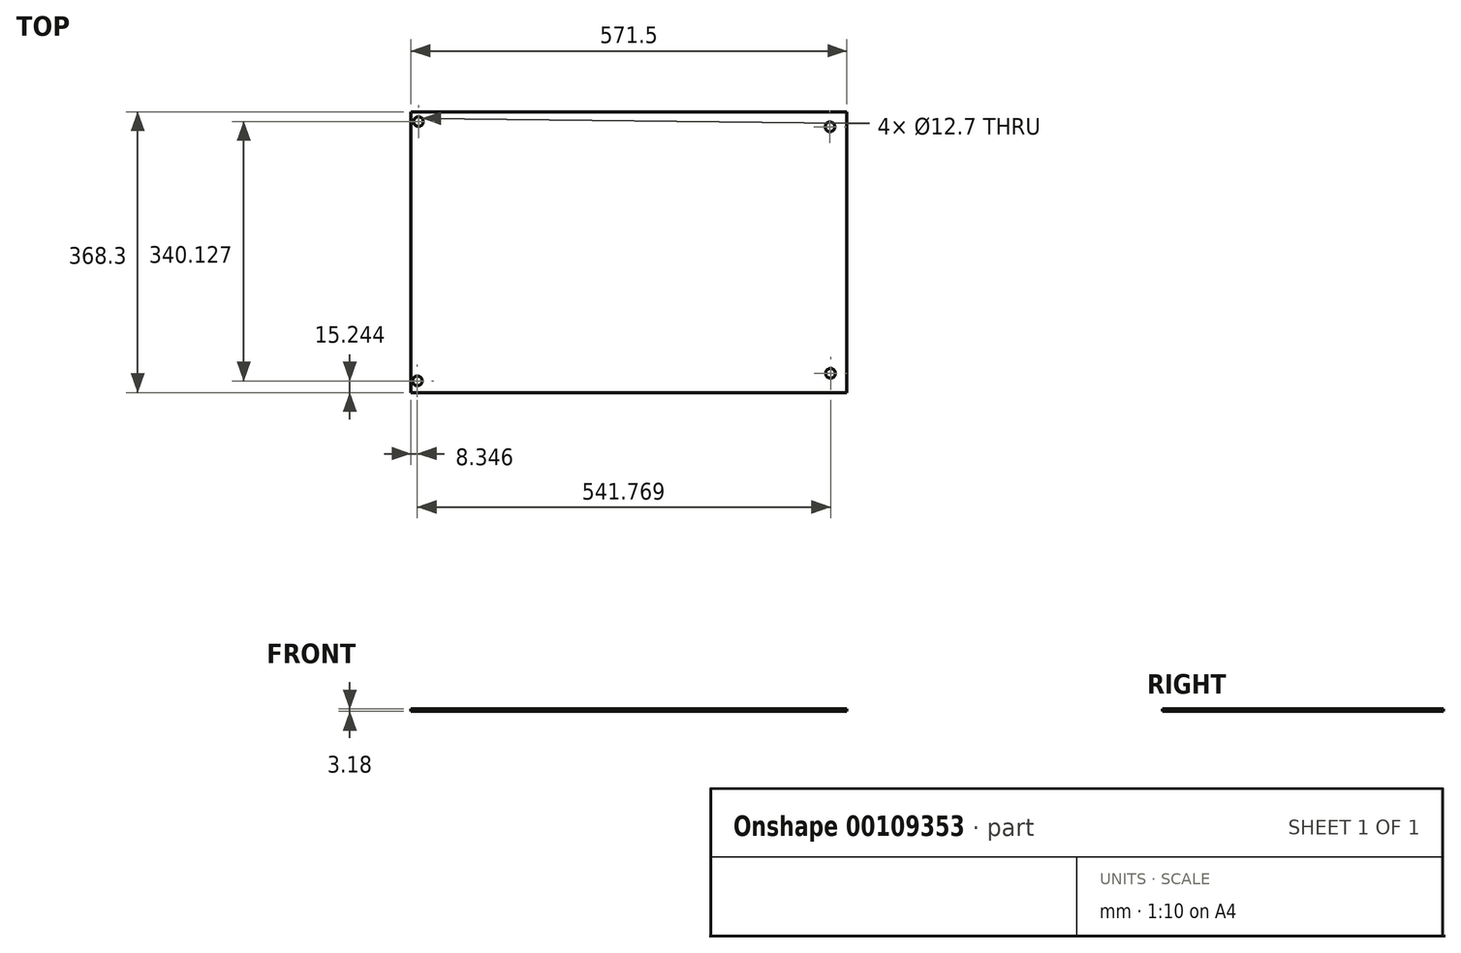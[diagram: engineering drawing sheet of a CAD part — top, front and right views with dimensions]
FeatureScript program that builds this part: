
annotation { "Feature Type Name" : "Feature", "Feature Type Description" : "" }
export const myFeature = defineFeature(function(context is Context, id is Id, definition is map)
    precondition{}
    {
        {
            var Q0;
            Q0=qCreatedBy(makeId("Top.planeOp"),FACE);
            var sketch = newSketch(context, id + "F0", { "sketchPlane" : qUnion([Q0])});
            skLineSegment(sketch, "E0.bottom", {"start": v(-280.24, 211) * mm, "end": v(291.26, 211) * mm});
            skLineSegment(sketch, "E0.top", {"start": v(-280.24, -157.3) * mm, "end": v(291.26, -157.3) * mm});
            skLineSegment(sketch, "E0.left", {"start": v(-280.24, 211) * mm, "end": v(-280.24, -157.3) * mm});
            skLineSegment(sketch, "E0.right", {"start": v(291.26, 211) * mm, "end": v(291.26, -157.3) * mm});
            skSolve(sketch);
        }
        {
            var Q0;
            Q0 = qSketchRegion(id + "F0", true);
            extrude(context, id + "F1", {"entities" : qUnion([Q0]), "depth" : 3.17 * mm});
        }
        {
            var Q0;
            Q0=makeQuery(id+"F1.opExtrude","CAP_FACE",FACE,{"disambiguationData":[OSD([sQuery(id+"F0.wireOp",EDGE,"E0.bottom"),sQuery(id+"F0.wireOp",EDGE,"E0.top"),sQuery(id+"F0.wireOp",EDGE,"E0.left"),sQuery(id+"F0.wireOp",EDGE,"E0.right")])],"isStart":false});
            var sketch = newSketch(context, id + "F2", { "sketchPlane" : qUnion([Q0])});
            skCircle(sketch, "E1", {"center": v(-271.9, -142.06) * mm, "radius": 6.35 * mm});
            skSolve(sketch);
        }
        {
            var Q0;
            Q0 = qSketchRegion(id + "F2", true);
            extrude(context, id + "F3", {"entities" : qUnion([Q0]), "operationType" : NewBodyOperationType.REMOVE, "oppositeDirection" : true, "depth" : 25.4 * mm});
        }
        {
            var Q0;
            Q0=makeQuery(id+"F1.opExtrude","CAP_FACE",FACE,{"disambiguationData":[OSD([sQuery(id+"F0.wireOp",EDGE,"E0.bottom"),sQuery(id+"F0.wireOp",EDGE,"E0.top"),sQuery(id+"F0.wireOp",EDGE,"E0.left"),sQuery(id+"F0.wireOp",EDGE,"E0.right")])],"isStart":false});
            var sketch = newSketch(context, id + "F4", { "sketchPlane" : qUnion([Q0])});
            skCircle(sketch, "E2", {"center": v(-270.44, 198.07) * mm, "radius": 6.35 * mm});
            skSolve(sketch);
        }
        {
            var Q0;
            Q0 = qSketchRegion(id + "F4", true);
            extrude(context, id + "F5", {"entities" : qUnion([Q0]), "operationType" : NewBodyOperationType.REMOVE, "oppositeDirection" : true, "depth" : 25.4 * mm});
        }
        {
            var Q0;
            Q0=makeQuery(id+"F1.opExtrude","CAP_FACE",FACE,{"disambiguationData":[OSD([sQuery(id+"F0.wireOp",EDGE,"E0.bottom"),sQuery(id+"F0.wireOp",EDGE,"E0.top"),sQuery(id+"F0.wireOp",EDGE,"E0.left"),sQuery(id+"F0.wireOp",EDGE,"E0.right")])],"isStart":false});
            var sketch = newSketch(context, id + "F6", { "sketchPlane" : qUnion([Q0])});
            skCircle(sketch, "E3", {"center": v(269.15, 191.22) * mm, "radius": 6.35 * mm});
            skSolve(sketch);
        }
        {
            var Q0;
            Q0 = qSketchRegion(id + "F6", true);
            extrude(context, id + "F7", {"entities" : qUnion([Q0]), "operationType" : NewBodyOperationType.REMOVE, "oppositeDirection" : true, "depth" : 25.4 * mm});
        }
        {
            var Q0;
            Q0=makeQuery(id+"F1.opExtrude","CAP_FACE",FACE,{"disambiguationData":[OSD([sQuery(id+"F0.wireOp",EDGE,"E0.bottom"),sQuery(id+"F0.wireOp",EDGE,"E0.top"),sQuery(id+"F0.wireOp",EDGE,"E0.left"),sQuery(id+"F0.wireOp",EDGE,"E0.right")])],"isStart":false});
            var sketch = newSketch(context, id + "F8", { "sketchPlane" : qUnion([Q0])});
            skCircle(sketch, "E4", {"center": v(269.87, -132.12) * mm, "radius": 6.35 * mm});
            skSolve(sketch);
        }
        {
            var Q0;
            Q0 = qSketchRegion(id + "F8", true);
            extrude(context, id + "F9", {"entities" : qUnion([Q0]), "operationType" : NewBodyOperationType.REMOVE, "oppositeDirection" : true, "depth" : 25.4 * mm});
        }
    });
